# Revit family: QF_ADVENTYS_OCTOPUS_PACK_1_250926092548
name_source: partatom
category: Specialty Equipment
units: mm (PartAtom-declared; Revit-internal decimal feet)

## family parameters
Always vertical = Yes
Cut with Voids When Loaded = No
OmniClass Number = 23.40.40.14
OmniClass Title = Food Service Equipment
Part Type = Normal
Room Calculation Point = No
Round Connector Dimension = Use Diameter
Shared = No
Work Plane-Based = No

## types (1)
- ADV1945
    Accessory = No
    Cost = 2215 $
    Default Elevation = 0 mm  [stored 0 ft]
    Depth Actual = 410 mm  [stored 1.34514 ft]
    Description = OCTOPUS PACK 1 INDUCTION BBQ
    Height Actual = 174 mm  [stored 0.570866 ft]
    Hot Water Consumption = 0.0 L/s
    Length Actual = 600 mm
    Manufacturer = ADVENTYS
    Model = OCTOPUS PACK 1
    URL = www.adventys.com
    Weight = 12.00 kg

note: [stored X ft] marks values corroborated as IEEE doubles in the binary element streams (Revit-internal decimal feet)

## geometry (parser evidence)
native form markers: Sweep x7
no freeform markers — native parametric forms only
